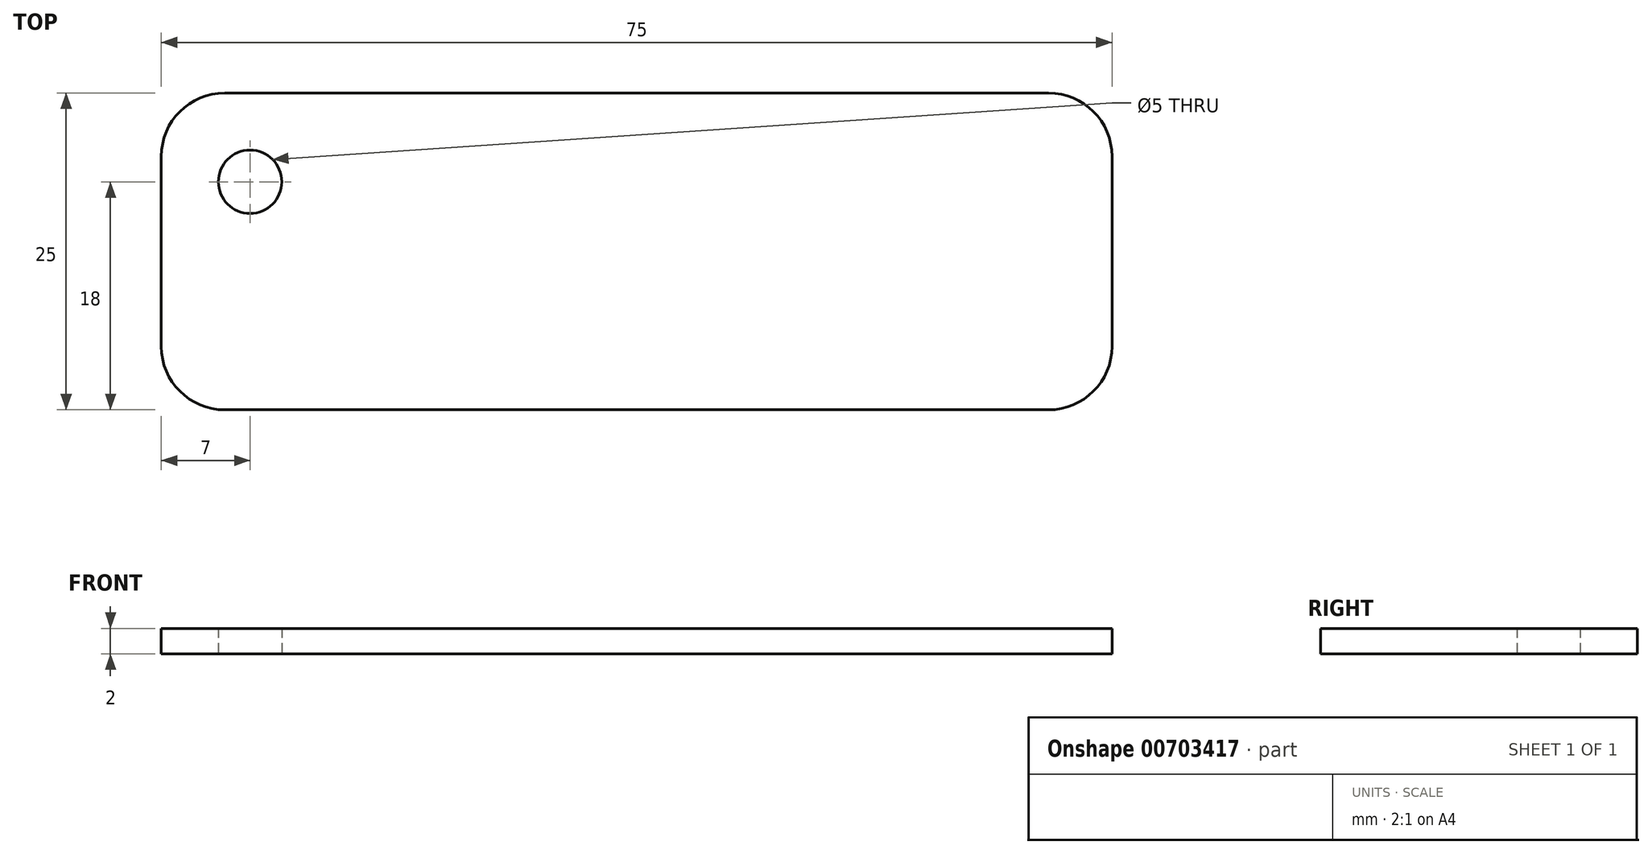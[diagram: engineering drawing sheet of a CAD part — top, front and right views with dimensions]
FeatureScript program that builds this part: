
annotation { "Feature Type Name" : "Feature", "Feature Type Description" : "" }
export const myFeature = defineFeature(function(context is Context, id is Id, definition is map)
    precondition{}
    {
        {
            var Q0;
            Q0=qCreatedBy(makeId("Top.planeOp"),FACE);
            var sketch = newSketch(context, id + "F0", { "sketchPlane" : qUnion([Q0])});
            skLineSegment(sketch, "E0.bottom", {"start": v(32.5, 12.5) * mm, "end": v(-32.5, 12.5) * mm});
            skLineSegment(sketch, "E0.top", {"start": v(32.5, -12.5) * mm, "end": v(-32.5, -12.5) * mm});
            skLineSegment(sketch, "E0.left", {"start": v(37.5, 7.5) * mm, "end": v(37.5, -7.5) * mm});
            skLineSegment(sketch, "E0.right", {"start": v(-37.5, 7.5) * mm, "end": v(-37.5, -7.5) * mm});
            skPoint(sketch, "E0.middle", {"position": v(0, 0) * mm});
            skPoint(sketch, "E1.visualSharp", {"position": v(-37.5, 12.5) * mm});
            skArc(sketch, "E1.filletArc", {"start": v(-32.5, 12.5) * mm, "mid": v(-36.04, 11.04) * mm, "end": v(-37.5, 7.5) * mm});
            skPoint(sketch, "E2.visualSharp", {"position": v(37.5, 12.5) * mm});
            skArc(sketch, "E2.filletArc", {"start": v(37.5, 7.5) * mm, "mid": v(36.04, 11.04) * mm, "end": v(32.5, 12.5) * mm});
            skPoint(sketch, "E3.visualSharp", {"position": v(37.5, -12.5) * mm});
            skArc(sketch, "E3.filletArc", {"start": v(32.5, -12.5) * mm, "mid": v(36.04, -11.04) * mm, "end": v(37.5, -7.5) * mm});
            skPoint(sketch, "E4.visualSharp", {"position": v(-37.5, -12.5) * mm});
            skArc(sketch, "E4.filletArc", {"start": v(-37.5, -7.5) * mm, "mid": v(-36.04, -11.04) * mm, "end": v(-32.5, -12.5) * mm});
            skSolve(sketch);
        }
        {
            var Q0;
            Q0=makeQuery(id+"F0.imprint","IMPRINT",FACE,{"disambiguationData":[TD([[makeQuery(id+"F0.imprint","IMPRINT",EDGE,{"derivedFrom":sQuery(id+"F0.wireOp",EDGE,"E0.bottom")}),1.0]])]});
            extrude(context, id + "F1", {"entities" : qUnion([Q0]), "depth" : 2 * mm, "offsetDistance" : 25 * mm});
        }
        {
            var Q0;
            Q0=qCreatedBy(makeId("Top.planeOp"),FACE);
            var sketch = newSketch(context, id + "F2", { "sketchPlane" : qUnion([Q0])});
            skPoint(sketch, "E5", {"position": v(-30.5, 5.5) * mm});
            skPoint(sketch, "E6", {"position": v(-30.45, 5.7) * mm});
            skSolve(sketch);
        }
        {
            var Q0;
            Q0=sQuery(id+"F2.wireOp",VERTEX,"E5");
            var Q1;
            Q1=makeQuery(id+"F1.opExtrude","SWEPT_BODY",BODY,{"disambiguationData":[OSD([sQuery(id+"F0.wireOp",EDGE,"E0.bottom"),sQuery(id+"F0.wireOp",EDGE,"E0.top"),sQuery(id+"F0.wireOp",EDGE,"E0.left"),sQuery(id+"F0.wireOp",EDGE,"E0.right"),sQuery(id+"F0.wireOp",EDGE,"E1.filletArc"),sQuery(id+"F0.wireOp",EDGE,"E2.filletArc"),sQuery(id+"F0.wireOp",EDGE,"E3.filletArc"),sQuery(id+"F0.wireOp",EDGE,"E4.filletArc")])]});
            hole(context, id + "F3", {"style" : HoleStyle.SIMPLE, "endStyle" : HoleEndStyle.THROUGH, "oppositeDirection" : true, "holeDiameter" : 5 * mm, "majorDiameter" : 5 * mm, "isTappedThrough" : true, "tappedDepth" : 12 * mm, "tapClearance" : 3, "locations" : qUnion([Q0]), "scope" : qUnion([Q1])});
        }
        {
            var Q0;
            Q0=qCreatedBy(makeId("Top.planeOp"),FACE);
            var sketch = newSketch(context, id + "F4", { "sketchPlane" : qUnion([Q0])});
            skText(sketch, "E7", { "text": "Torin", "fontName": "OpenSans-Regular.ttf"});
            const initialGuessF4  = {"E7": [-0.01815, 0, 1, 0, 0.0111]};
            skSetInitialGuess(sketch, initialGuessF4);
            skSolve(sketch);
        }
        {
            var Q0;
            Q0 = qSketchRegion(id + "F4", true);
            extrude(context, id + "F5", {"entities" : qUnion([Q0]), "operationType" : NewBodyOperationType.ADD, "depth" : 1 * mm, "offsetDistance" : 25 * mm});
        }
    });
